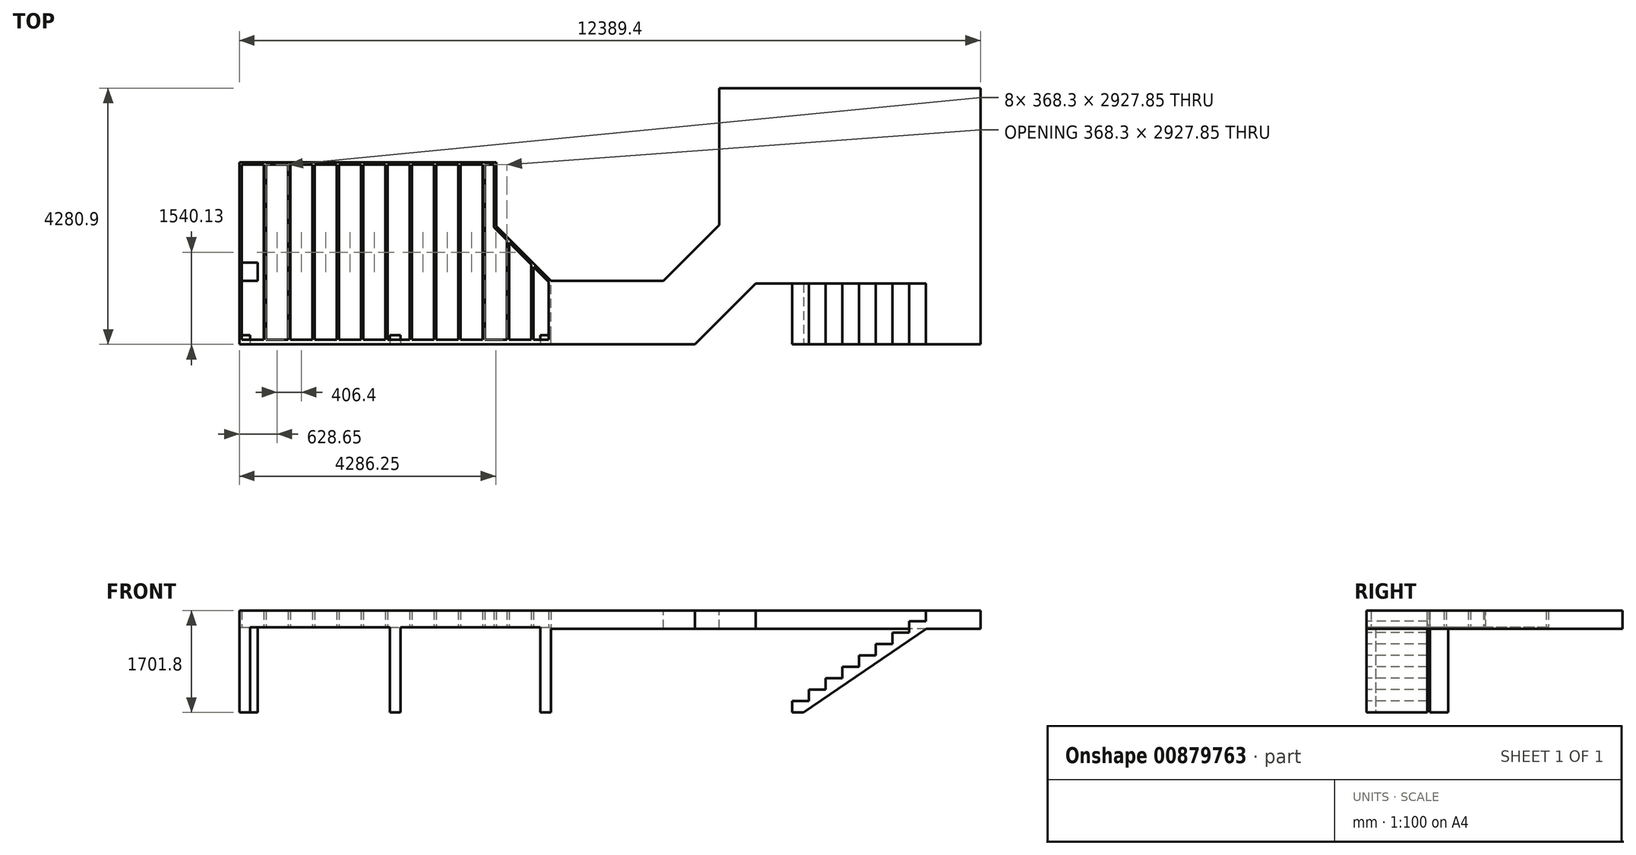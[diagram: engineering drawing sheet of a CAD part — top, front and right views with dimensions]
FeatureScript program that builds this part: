
annotation { "Feature Type Name" : "Feature", "Feature Type Description" : "" }
export const myFeature = defineFeature(function(context is Context, id is Id, definition is map)
    precondition{}
    {
        {
            var Q0;
            Q0=qCreatedBy(makeId("Top.planeOp"),FACE);
            var sketch = newSketch(context, id + "F0", { "sketchPlane" : qUnion([Q0])});
            skLineSegment(sketch, "E0.bottom", {"start": v(0, -1676.4) * mm, "end": v(304.8, -1676.4) * mm});
            skLineSegment(sketch, "E0.top", {"start": v(0, -1981.2) * mm, "end": v(304.8, -1981.2) * mm});
            skLineSegment(sketch, "E0.left", {"start": v(0, -1676.4) * mm, "end": v(0, -1981.2) * mm});
            skLineSegment(sketch, "E0.right", {"start": v(304.8, -1676.4) * mm, "end": v(304.8, -1981.2) * mm});
            skLineSegment(sketch, "E1.bottom", {"start": v(0, -2889.75) * mm, "end": v(177.8, -2889.75) * mm});
            skLineSegment(sketch, "E1.top", {"start": v(0, -3042.15) * mm, "end": v(177.8, -3042.15) * mm});
            skLineSegment(sketch, "E1.left", {"start": v(0, -2889.75) * mm, "end": v(0, -3042.15) * mm});
            skLineSegment(sketch, "E1.right", {"start": v(177.8, -2889.75) * mm, "end": v(177.8, -3042.15) * mm});
            skLineSegment(sketch, "E2.bottom", {"start": v(2514.6, -2889.75) * mm, "end": v(2692.4, -2889.75) * mm});
            skLineSegment(sketch, "E2.top", {"start": v(2514.6, -3042.15) * mm, "end": v(2692.4, -3042.15) * mm});
            skLineSegment(sketch, "E2.left", {"start": v(2514.6, -2889.75) * mm, "end": v(2514.6, -3042.15) * mm});
            skLineSegment(sketch, "E2.right", {"start": v(2692.4, -2889.75) * mm, "end": v(2692.4, -3042.15) * mm});
            skLineSegment(sketch, "E3.bottom", {"start": v(5029.2, -2889.75) * mm, "end": v(5207, -2889.75) * mm});
            skLineSegment(sketch, "E3.top", {"start": v(5029.2, -3042.15) * mm, "end": v(5207, -3042.15) * mm});
            skLineSegment(sketch, "E3.left", {"start": v(5029.2, -2889.75) * mm, "end": v(5029.2, -3042.15) * mm});
            skLineSegment(sketch, "E3.right", {"start": v(5207, -2889.75) * mm, "end": v(5207, -3042.15) * mm});
            skLineSegment(sketch, "E4", {"start": v(0, 0) * mm, "end": v(4292.6, 0) * mm, "construction": true});
            skLineSegment(sketch, "E5", {"start": v(4292.6, 0) * mm, "end": v(4292.6, -1066.8) * mm, "construction": true});
            skLineSegment(sketch, "E6", {"start": v(4292.6, -1066.8) * mm, "end": v(5226.55, -2000.75) * mm, "construction": true});
            skLineSegment(sketch, "E7", {"start": v(5226.55, -2000.75) * mm, "end": v(7106.15, -2000.75) * mm, "construction": true});
            skSolve(sketch);
        }
        {
            var Q0;
            Q0=qSketchRegion(id+"F0",true);
            extrude(context, id + "F1", {"entities" : qUnion([Q0]), "depth" : 1422.4 * mm, "offsetDistance" : 25.4 * mm});
        }
        {
            var Q0;
            Q0=makeQuery(id+"F1.opExtrude","CAP_FACE",FACE,{"disambiguationData":[OSD([sQuery(id+"F0.wireOp",EDGE,"E0.bottom"),sQuery(id+"F0.wireOp",EDGE,"E0.top"),sQuery(id+"F0.wireOp",EDGE,"E0.left"),sQuery(id+"F0.wireOp",EDGE,"E0.right")])],"isStart":false});
            var sketch = newSketch(context, id + "F2", { "sketchPlane" : qUnion([Q0])});
            skLineSegment(sketch, "E8.0", {"start": v(0, 0) * mm, "end": v(4292.6, 0) * mm});
            skLineSegment(sketch, "E9.0", {"start": v(4292.6, 0) * mm, "end": v(4292.6, -1066.8) * mm});
            skLineSegment(sketch, "E9.1", {"start": v(4292.6, -1066.8) * mm, "end": v(5207, -1981.2) * mm});
            skLineSegment(sketch, "E10", {"start": v(0, 0) * mm, "end": v(0, -3042.15) * mm});
            skLineSegment(sketch, "E11", {"start": v(0, -3042.15) * mm, "end": v(5207, -3042.15) * mm});
            skLineSegment(sketch, "E12", {"start": v(5207, -3042.15) * mm, "end": v(5207, -1981.2) * mm});
            skPoint(sketch, "E13.orphan", {"position": v(5226.55, -2000.75) * mm});
            skLineSegment(sketch, "E14.0", {"start": v(4254.5, -38.1) * mm, "end": v(4254.5, -1082.58) * mm});
            skLineSegment(sketch, "E14.1", {"start": v(5168.9, -3004.05) * mm, "end": v(5168.9, -1996.98) * mm});
            skLineSegment(sketch, "E14.2", {"start": v(38.1, -3004.05) * mm, "end": v(5168.9, -3004.05) * mm});
            skLineSegment(sketch, "E14.3", {"start": v(4254.5, -1082.58) * mm, "end": v(5168.9, -1996.98) * mm});
            skLineSegment(sketch, "E14.4", {"start": v(38.1, -38.1) * mm, "end": v(38.1, -3004.05) * mm});
            skLineSegment(sketch, "E14.5", {"start": v(38.1, -38.1) * mm, "end": v(4254.5, -38.1) * mm});
            skSolve(sketch);
        }
        {
            var Q0;
            Q0=qSketchRegion(id+"F2",true);
            extrude(context, id + "F3", {"entities" : qUnion([Q0]), "operationType" : NewBodyOperationType.ADD, "depth" : 279.4 * mm, "offsetDistance" : 25.4 * mm});
        }
        {
            var Q0;
            Q0=makeQuery(id+"F1.opExtrude","CAP_FACE",FACE,{"disambiguationData":[OSD([sQuery(id+"F0.wireOp",EDGE,"E1.bottom"),sQuery(id+"F0.wireOp",EDGE,"E1.top"),sQuery(id+"F0.wireOp",EDGE,"E1.left"),sQuery(id+"F0.wireOp",EDGE,"E1.right")])],"isStart":false});
            var sketch = newSketch(context, id + "F4", { "sketchPlane" : qUnion([Q0])});
            skPoint(sketch, "E15.oppositeSnap0", {"position": v(38.1, -2965.95) * mm});
            skLineSegment(sketch, "E15.bottom", {"start": v(38.1, -3004.05) * mm, "end": v(5168.9, -3004.05) * mm});
            skLineSegment(sketch, "E15.top", {"start": v(38.1, -2965.95) * mm, "end": v(5168.9, -2965.95) * mm});
            skLineSegment(sketch, "E15.left", {"start": v(38.1, -3004.05) * mm, "end": v(38.1, -2965.95) * mm});
            skLineSegment(sketch, "E15.right", {"start": v(5168.9, -3004.05) * mm, "end": v(5168.9, -2965.95) * mm});
            skSolve(sketch);
        }
        {
            var Q0;
            Q0=qSketchRegion(id+"F4",true);
            var Q1;
            Q1=makeQuery(id+"F3.opExtrude","CAP_FACE",FACE,{"disambiguationData":[OSD([sQuery(id+"F2.wireOp",EDGE,"E8.0"),sQuery(id+"F2.wireOp",EDGE,"E9.0"),sQuery(id+"F2.wireOp",EDGE,"E9.1"),sQuery(id+"F2.wireOp",EDGE,"E10"),sQuery(id+"F2.wireOp",EDGE,"E11"),sQuery(id+"F2.wireOp",EDGE,"E12"),sQuery(id+"F2.wireOp",EDGE,"E14.0"),sQuery(id+"F2.wireOp",EDGE,"E14.1"),sQuery(id+"F2.wireOp",EDGE,"E14.2"),sQuery(id+"F2.wireOp",EDGE,"E14.3"),sQuery(id+"F2.wireOp",EDGE,"E14.4"),sQuery(id+"F2.wireOp",EDGE,"E14.5")])],"isStart":false});
            extrude(context, id + "F5", {"entities" : qUnion([Q0]), "operationType" : NewBodyOperationType.ADD, "endBound" : BoundingType.UP_TO_SURFACE, "depth" : 25.4 * mm, "endBoundEntityFace" : qUnion([Q1]), "offsetDistance" : 25.4 * mm});
        }
        {
            var Q0;
            Q0=makeQuery(id+"F1.opExtrude","CAP_FACE",FACE,{"disambiguationData":[OSD([sQuery(id+"F0.wireOp",EDGE,"E0.bottom"),sQuery(id+"F0.wireOp",EDGE,"E0.top"),sQuery(id+"F0.wireOp",EDGE,"E0.left"),sQuery(id+"F0.wireOp",EDGE,"E0.right")])],"isStart":false});
            var sketch = newSketch(context, id + "F6", { "sketchPlane" : qUnion([Q0])});
            skLineSegment(sketch, "E16.bottom", {"start": v(406.4, -38.1) * mm, "end": v(444.5, -38.1) * mm});
            skLineSegment(sketch, "E16.top", {"start": v(406.4, -2965.95) * mm, "end": v(444.5, -2965.95) * mm});
            skLineSegment(sketch, "E16.left", {"start": v(406.4, -38.1) * mm, "end": v(406.4, -2965.95) * mm});
            skLineSegment(sketch, "E16.right", {"start": v(444.5, -38.1) * mm, "end": v(444.5, -2965.95) * mm});
            skLineSegment(sketch, "E17.1.0.0", {"start": v(850.9, -38.1) * mm, "end": v(850.9, -2965.95) * mm});
            skLineSegment(sketch, "E17.1.0.1", {"start": v(812.8, -38.1) * mm, "end": v(812.8, -2965.95) * mm});
            skLineSegment(sketch, "E17.1.0.2", {"start": v(812.8, -38.1) * mm, "end": v(850.9, -38.1) * mm});
            skLineSegment(sketch, "E17.1.0.3", {"start": v(812.8, -2965.95) * mm, "end": v(850.9, -2965.95) * mm});
            skLineSegment(sketch, "E17.2.0.0", {"start": v(1257.3, -38.1) * mm, "end": v(1257.3, -2965.95) * mm});
            skLineSegment(sketch, "E17.2.0.1", {"start": v(1219.2, -38.1) * mm, "end": v(1219.2, -2965.95) * mm});
            skLineSegment(sketch, "E17.2.0.2", {"start": v(1219.2, -38.1) * mm, "end": v(1257.3, -38.1) * mm});
            skLineSegment(sketch, "E17.2.0.3", {"start": v(1219.2, -2965.95) * mm, "end": v(1257.3, -2965.95) * mm});
            skLineSegment(sketch, "E17.3.0.0", {"start": v(1663.7, -38.1) * mm, "end": v(1663.7, -2965.95) * mm});
            skLineSegment(sketch, "E17.3.0.1", {"start": v(1625.6, -38.1) * mm, "end": v(1625.6, -2965.95) * mm});
            skLineSegment(sketch, "E17.3.0.2", {"start": v(1625.6, -38.1) * mm, "end": v(1663.7, -38.1) * mm});
            skLineSegment(sketch, "E17.3.0.3", {"start": v(1625.6, -2965.95) * mm, "end": v(1663.7, -2965.95) * mm});
            skLineSegment(sketch, "E17.4.0.0", {"start": v(2070.1, -38.1) * mm, "end": v(2070.1, -2965.95) * mm});
            skLineSegment(sketch, "E17.4.0.1", {"start": v(2032, -38.1) * mm, "end": v(2032, -2965.95) * mm});
            skLineSegment(sketch, "E17.4.0.2", {"start": v(2032, -38.1) * mm, "end": v(2070.1, -38.1) * mm});
            skLineSegment(sketch, "E17.4.0.3", {"start": v(2032, -2965.95) * mm, "end": v(2070.1, -2965.95) * mm});
            skLineSegment(sketch, "E17.5.0.0", {"start": v(2476.5, -38.1) * mm, "end": v(2476.5, -2965.95) * mm});
            skLineSegment(sketch, "E17.5.0.1", {"start": v(2438.4, -38.1) * mm, "end": v(2438.4, -2965.95) * mm});
            skLineSegment(sketch, "E17.5.0.2", {"start": v(2438.4, -38.1) * mm, "end": v(2476.5, -38.1) * mm});
            skLineSegment(sketch, "E17.5.0.3", {"start": v(2438.4, -2965.95) * mm, "end": v(2476.5, -2965.95) * mm});
            skLineSegment(sketch, "E17.6.0.0", {"start": v(2882.9, -38.1) * mm, "end": v(2882.9, -2965.95) * mm});
            skLineSegment(sketch, "E17.6.0.1", {"start": v(2844.8, -38.1) * mm, "end": v(2844.8, -2965.95) * mm});
            skLineSegment(sketch, "E17.6.0.2", {"start": v(2844.8, -38.1) * mm, "end": v(2882.9, -38.1) * mm});
            skLineSegment(sketch, "E17.6.0.3", {"start": v(2844.8, -2965.95) * mm, "end": v(2882.9, -2965.95) * mm});
            skLineSegment(sketch, "E17.7.0.0", {"start": v(3289.3, -38.1) * mm, "end": v(3289.3, -2965.95) * mm});
            skLineSegment(sketch, "E17.7.0.1", {"start": v(3251.2, -38.1) * mm, "end": v(3251.2, -2965.95) * mm});
            skLineSegment(sketch, "E17.7.0.2", {"start": v(3251.2, -38.1) * mm, "end": v(3289.3, -38.1) * mm});
            skLineSegment(sketch, "E17.7.0.3", {"start": v(3251.2, -2965.95) * mm, "end": v(3289.3, -2965.95) * mm});
            skLineSegment(sketch, "E17.8.0.0", {"start": v(3695.7, -38.1) * mm, "end": v(3695.7, -2965.95) * mm});
            skLineSegment(sketch, "E17.8.0.1", {"start": v(3657.6, -38.1) * mm, "end": v(3657.6, -2965.95) * mm});
            skLineSegment(sketch, "E17.8.0.2", {"start": v(3657.6, -38.1) * mm, "end": v(3695.7, -38.1) * mm});
            skLineSegment(sketch, "E17.8.0.3", {"start": v(3657.6, -2965.95) * mm, "end": v(3695.7, -2965.95) * mm});
            skLineSegment(sketch, "E17.9.0.0", {"start": v(4102.1, -38.1) * mm, "end": v(4102.1, -2965.95) * mm});
            skLineSegment(sketch, "E17.9.0.1", {"start": v(4064, -38.1) * mm, "end": v(4064, -2965.95) * mm});
            skLineSegment(sketch, "E17.9.0.2", {"start": v(4064, -38.1) * mm, "end": v(4102.1, -38.1) * mm});
            skLineSegment(sketch, "E17.9.0.3", {"start": v(4064, -2965.95) * mm, "end": v(4102.1, -2965.95) * mm});
            skLineSegment(sketch, "E17.direction1", {"start": v(406.4, -2965.95) * mm, "end": v(812.8, -2965.95) * mm, "construction": true});
            skLineSegment(sketch, "E18.top", {"start": v(4470.4, -2965.95) * mm, "end": v(4508.5, -2965.95) * mm});
            skLineSegment(sketch, "E18.left", {"start": v(4470.4, -1298.48) * mm, "end": v(4470.4, -2965.95) * mm});
            skLineSegment(sketch, "E18.right", {"start": v(4508.5, -1336.58) * mm, "end": v(4508.5, -2965.95) * mm});
            skLineSegment(sketch, "E19.top", {"start": v(4876.8, -2965.95) * mm, "end": v(4914.9, -2965.95) * mm});
            skLineSegment(sketch, "E19.left", {"start": v(4876.8, -1704.88) * mm, "end": v(4876.8, -2965.95) * mm});
            skLineSegment(sketch, "E19.right", {"start": v(4914.9, -1742.98) * mm, "end": v(4914.9, -2965.95) * mm});
            skLineSegment(sketch, "E20", {"start": v(4470.4, -1298.48) * mm, "end": v(4508.5, -1336.58) * mm});
            skLineSegment(sketch, "E21.trimOffspring", {"start": v(4876.8, -1704.88) * mm, "end": v(4914.9, -1742.98) * mm});
            skSolve(sketch);
        }
        {
            var Q0;
            Q0=qSketchRegion(id+"F6",true);
            var Q1;
            {var subQ0=sQuery(id+"F2.wireOp",EDGE,"E14.5");var subQ1=sQuery(id+"F2.wireOp",EDGE,"E14.4");var subQ2=sQuery(id+"F2.wireOp",EDGE,"E14.3");var subQ3=sQuery(id+"F2.wireOp",EDGE,"E14.2");var subQ4=sQuery(id+"F2.wireOp",EDGE,"E14.1");var subQ5=sQuery(id+"F2.wireOp",EDGE,"E14.0");var subQ6=sQuery(id+"F2.wireOp",EDGE,"E12");var subQ7=sQuery(id+"F2.wireOp",EDGE,"E11");var subQ8=sQuery(id+"F2.wireOp",EDGE,"E10");var subQ9=sQuery(id+"F2.wireOp",EDGE,"E9.1");var subQ10=sQuery(id+"F2.wireOp",EDGE,"E9.0");var subQ11=sQuery(id+"F2.wireOp",EDGE,"E8.0");Q1=makeQuery(id+"F5.boolean.opBoolean","MERGE",FACE,{"derivedFrom":[makeQuery(id+"F3.opExtrude","CAP_FACE",FACE,{"disambiguationData":[OSD([subQ11,subQ10,subQ9,subQ8,subQ7,subQ6,subQ5,subQ4,subQ3,subQ2,subQ1,subQ0])],"isStart":false}),makeQuery(id+"F5.opExtrude","CAP_FACE",FACE,{"disambiguationData":[OSD([subQ11,subQ10,subQ9,subQ8,subQ7,subQ6,subQ5,subQ4,subQ3,subQ2,subQ1,subQ0])],"isStart":false})]});}
            extrude(context, id + "F7", {"entities" : qUnion([Q0]), "operationType" : NewBodyOperationType.ADD, "endBound" : BoundingType.UP_TO_SURFACE, "depth" : 25.4 * mm, "endBoundEntityFace" : qUnion([Q1]), "offsetDistance" : 25.4 * mm});
        }
        {
            var Q0;
            Q0=makeQuery(id+"F7.boolean.opBoolean","MERGE",FACE,{"derivedFrom":[makeQuery(id+"F5.boolean.opBoolean","MERGE",FACE,{"derivedFrom":[makeQuery(id+"F3.opExtrude","CAP_FACE",FACE,{"disambiguationData":[OSD([sQuery(id+"F2.wireOp",EDGE,"E8.0"),sQuery(id+"F2.wireOp",EDGE,"E9.0"),sQuery(id+"F2.wireOp",EDGE,"E9.1"),sQuery(id+"F2.wireOp",EDGE,"E10"),sQuery(id+"F2.wireOp",EDGE,"E11"),sQuery(id+"F2.wireOp",EDGE,"E12"),sQuery(id+"F2.wireOp",EDGE,"E14.0"),sQuery(id+"F2.wireOp",EDGE,"E14.1"),sQuery(id+"F2.wireOp",EDGE,"E14.2"),sQuery(id+"F2.wireOp",EDGE,"E14.3"),sQuery(id+"F2.wireOp",EDGE,"E14.4"),sQuery(id+"F2.wireOp",EDGE,"E14.5")])],"isStart":false}),makeQuery(id+"F5.opExtrude","CAP_FACE",FACE,{"disambiguationData":[OSD([sQuery(id+"F4.wireOp",EDGE,"E15.bottom"),sQuery(id+"F4.wireOp",EDGE,"E15.top"),sQuery(id+"F4.wireOp",EDGE,"E15.left"),sQuery(id+"F4.wireOp",EDGE,"E15.right")])],"isStart":false})]}),makeQuery(id+"F7.opExtrude","CAP_FACE",FACE,{"disambiguationData":[OSD([sQuery(id+"F6.wireOp",EDGE,"E16.bottom"),sQuery(id+"F6.wireOp",EDGE,"E16.top"),sQuery(id+"F6.wireOp",EDGE,"E16.left"),sQuery(id+"F6.wireOp",EDGE,"E16.right")])],"isStart":false}),makeQuery(id+"F7.opExtrude","CAP_FACE",FACE,{"disambiguationData":[OSD([sQuery(id+"F6.wireOp",EDGE,"E17.1.0.0"),sQuery(id+"F6.wireOp",EDGE,"E17.1.0.1"),sQuery(id+"F6.wireOp",EDGE,"E17.1.0.2"),sQuery(id+"F6.wireOp",EDGE,"E17.1.0.3")])],"isStart":false}),makeQuery(id+"F7.opExtrude","CAP_FACE",FACE,{"disambiguationData":[OSD([sQuery(id+"F6.wireOp",EDGE,"E17.2.0.0"),sQuery(id+"F6.wireOp",EDGE,"E17.2.0.1"),sQuery(id+"F6.wireOp",EDGE,"E17.2.0.2"),sQuery(id+"F6.wireOp",EDGE,"E17.2.0.3")])],"isStart":false}),makeQuery(id+"F7.opExtrude","CAP_FACE",FACE,{"disambiguationData":[OSD([sQuery(id+"F6.wireOp",EDGE,"E17.3.0.0"),sQuery(id+"F6.wireOp",EDGE,"E17.3.0.1"),sQuery(id+"F6.wireOp",EDGE,"E17.3.0.2"),sQuery(id+"F6.wireOp",EDGE,"E17.3.0.3")])],"isStart":false}),makeQuery(id+"F7.opExtrude","CAP_FACE",FACE,{"disambiguationData":[OSD([sQuery(id+"F6.wireOp",EDGE,"E17.4.0.0"),sQuery(id+"F6.wireOp",EDGE,"E17.4.0.1"),sQuery(id+"F6.wireOp",EDGE,"E17.4.0.2"),sQuery(id+"F6.wireOp",EDGE,"E17.4.0.3")])],"isStart":false}),makeQuery(id+"F7.opExtrude","CAP_FACE",FACE,{"disambiguationData":[OSD([sQuery(id+"F6.wireOp",EDGE,"E17.5.0.0"),sQuery(id+"F6.wireOp",EDGE,"E17.5.0.1"),sQuery(id+"F6.wireOp",EDGE,"E17.5.0.2"),sQuery(id+"F6.wireOp",EDGE,"E17.5.0.3")])],"isStart":false}),makeQuery(id+"F7.opExtrude","CAP_FACE",FACE,{"disambiguationData":[OSD([sQuery(id+"F6.wireOp",EDGE,"E17.6.0.0"),sQuery(id+"F6.wireOp",EDGE,"E17.6.0.1"),sQuery(id+"F6.wireOp",EDGE,"E17.6.0.2"),sQuery(id+"F6.wireOp",EDGE,"E17.6.0.3")])],"isStart":false}),makeQuery(id+"F7.opExtrude","CAP_FACE",FACE,{"disambiguationData":[OSD([sQuery(id+"F6.wireOp",EDGE,"E17.7.0.0"),sQuery(id+"F6.wireOp",EDGE,"E17.7.0.1"),sQuery(id+"F6.wireOp",EDGE,"E17.7.0.2"),sQuery(id+"F6.wireOp",EDGE,"E17.7.0.3")])],"isStart":false}),makeQuery(id+"F7.opExtrude","CAP_FACE",FACE,{"disambiguationData":[OSD([sQuery(id+"F6.wireOp",EDGE,"E17.8.0.0"),sQuery(id+"F6.wireOp",EDGE,"E17.8.0.1"),sQuery(id+"F6.wireOp",EDGE,"E17.8.0.2"),sQuery(id+"F6.wireOp",EDGE,"E17.8.0.3")])],"isStart":false}),makeQuery(id+"F7.opExtrude","CAP_FACE",FACE,{"disambiguationData":[OSD([sQuery(id+"F6.wireOp",EDGE,"E17.9.0.0"),sQuery(id+"F6.wireOp",EDGE,"E17.9.0.1"),sQuery(id+"F6.wireOp",EDGE,"E17.9.0.2"),sQuery(id+"F6.wireOp",EDGE,"E17.9.0.3")])],"isStart":false}),makeQuery(id+"F7.opExtrude","CAP_FACE",FACE,{"disambiguationData":[OSD([sQuery(id+"F6.wireOp",EDGE,"E18.top"),sQuery(id+"F6.wireOp",EDGE,"E18.left"),sQuery(id+"F6.wireOp",EDGE,"E18.right"),sQuery(id+"F6.wireOp",EDGE,"E20")])],"isStart":false}),makeQuery(id+"F7.opExtrude","CAP_FACE",FACE,{"disambiguationData":[OSD([sQuery(id+"F6.wireOp",EDGE,"E19.top"),sQuery(id+"F6.wireOp",EDGE,"E19.left"),sQuery(id+"F6.wireOp",EDGE,"E19.right"),sQuery(id+"F6.wireOp",EDGE,"E21.trimOffspring")])],"isStart":false})]});
            var sketch = newSketch(context, id + "F8", { "sketchPlane" : qUnion([Q0])});
            skLineSegment(sketch, "E22", {"start": v(5207, -1981.2) * mm, "end": v(5207, -3042.15) * mm});
            skLineSegment(sketch, "E23", {"start": v(5207, -1981.2) * mm, "end": v(7086.6, -1981.2) * mm});
            skLineSegment(sketch, "E24", {"start": v(7086.6, -1981.2) * mm, "end": v(8020.55, -1047.25) * mm});
            skLineSegment(sketch, "E25", {"start": v(8020.55, -1047.25) * mm, "end": v(8020.55, 1238.75) * mm});
            skLineSegment(sketch, "E26", {"start": v(8020.55, 1238.75) * mm, "end": v(12389.35, 1238.75) * mm});
            skLineSegment(sketch, "E27", {"start": v(12389.35, 1238.75) * mm, "end": v(12389.35, -3042.15) * mm});
            skLineSegment(sketch, "E28", {"start": v(5207, -3042.15) * mm, "end": v(12389.35, -3042.15) * mm});
            skSolve(sketch);
        }
        {
            var Q0;
            Q0=qSketchRegion(id+"F8",true);
            extrude(context, id + "F9", {"entities" : qUnion([Q0]), "operationType" : NewBodyOperationType.ADD, "oppositeDirection" : true, "depth" : 304.8 * mm, "offsetDistance" : 25.4 * mm});
        }
        {
            var Q0;
            Q0=makeQuery(id+"F9.boolean.opBoolean","MERGE",FACE,{"derivedFrom":[makeQuery(id+"F7.boolean.opBoolean","MERGE",FACE,{"derivedFrom":[makeQuery(id+"F5.boolean.opBoolean","MERGE",FACE,{"derivedFrom":[makeQuery(id+"F3.opExtrude","CAP_FACE",FACE,{"disambiguationData":[OSD([sQuery(id+"F2.wireOp",EDGE,"E8.0"),sQuery(id+"F2.wireOp",EDGE,"E9.0"),sQuery(id+"F2.wireOp",EDGE,"E9.1"),sQuery(id+"F2.wireOp",EDGE,"E10"),sQuery(id+"F2.wireOp",EDGE,"E11"),sQuery(id+"F2.wireOp",EDGE,"E12"),sQuery(id+"F2.wireOp",EDGE,"E14.0"),sQuery(id+"F2.wireOp",EDGE,"E14.1"),sQuery(id+"F2.wireOp",EDGE,"E14.2"),sQuery(id+"F2.wireOp",EDGE,"E14.3"),sQuery(id+"F2.wireOp",EDGE,"E14.4"),sQuery(id+"F2.wireOp",EDGE,"E14.5")])],"isStart":false}),makeQuery(id+"F5.opExtrude","CAP_FACE",FACE,{"disambiguationData":[OSD([sQuery(id+"F4.wireOp",EDGE,"E15.bottom"),sQuery(id+"F4.wireOp",EDGE,"E15.top"),sQuery(id+"F4.wireOp",EDGE,"E15.left"),sQuery(id+"F4.wireOp",EDGE,"E15.right")])],"isStart":false})]}),makeQuery(id+"F7.opExtrude","CAP_FACE",FACE,{"disambiguationData":[OSD([sQuery(id+"F6.wireOp",EDGE,"E16.bottom"),sQuery(id+"F6.wireOp",EDGE,"E16.top"),sQuery(id+"F6.wireOp",EDGE,"E16.left"),sQuery(id+"F6.wireOp",EDGE,"E16.right")])],"isStart":false}),makeQuery(id+"F7.opExtrude","CAP_FACE",FACE,{"disambiguationData":[OSD([sQuery(id+"F6.wireOp",EDGE,"E17.1.0.0"),sQuery(id+"F6.wireOp",EDGE,"E17.1.0.1"),sQuery(id+"F6.wireOp",EDGE,"E17.1.0.2"),sQuery(id+"F6.wireOp",EDGE,"E17.1.0.3")])],"isStart":false}),makeQuery(id+"F7.opExtrude","CAP_FACE",FACE,{"disambiguationData":[OSD([sQuery(id+"F6.wireOp",EDGE,"E17.2.0.0"),sQuery(id+"F6.wireOp",EDGE,"E17.2.0.1"),sQuery(id+"F6.wireOp",EDGE,"E17.2.0.2"),sQuery(id+"F6.wireOp",EDGE,"E17.2.0.3")])],"isStart":false}),makeQuery(id+"F7.opExtrude","CAP_FACE",FACE,{"disambiguationData":[OSD([sQuery(id+"F6.wireOp",EDGE,"E17.3.0.0"),sQuery(id+"F6.wireOp",EDGE,"E17.3.0.1"),sQuery(id+"F6.wireOp",EDGE,"E17.3.0.2"),sQuery(id+"F6.wireOp",EDGE,"E17.3.0.3")])],"isStart":false}),makeQuery(id+"F7.opExtrude","CAP_FACE",FACE,{"disambiguationData":[OSD([sQuery(id+"F6.wireOp",EDGE,"E17.4.0.0"),sQuery(id+"F6.wireOp",EDGE,"E17.4.0.1"),sQuery(id+"F6.wireOp",EDGE,"E17.4.0.2"),sQuery(id+"F6.wireOp",EDGE,"E17.4.0.3")])],"isStart":false}),makeQuery(id+"F7.opExtrude","CAP_FACE",FACE,{"disambiguationData":[OSD([sQuery(id+"F6.wireOp",EDGE,"E17.5.0.0"),sQuery(id+"F6.wireOp",EDGE,"E17.5.0.1"),sQuery(id+"F6.wireOp",EDGE,"E17.5.0.2"),sQuery(id+"F6.wireOp",EDGE,"E17.5.0.3")])],"isStart":false}),makeQuery(id+"F7.opExtrude","CAP_FACE",FACE,{"disambiguationData":[OSD([sQuery(id+"F6.wireOp",EDGE,"E17.6.0.0"),sQuery(id+"F6.wireOp",EDGE,"E17.6.0.1"),sQuery(id+"F6.wireOp",EDGE,"E17.6.0.2"),sQuery(id+"F6.wireOp",EDGE,"E17.6.0.3")])],"isStart":false}),makeQuery(id+"F7.opExtrude","CAP_FACE",FACE,{"disambiguationData":[OSD([sQuery(id+"F6.wireOp",EDGE,"E17.7.0.0"),sQuery(id+"F6.wireOp",EDGE,"E17.7.0.1"),sQuery(id+"F6.wireOp",EDGE,"E17.7.0.2"),sQuery(id+"F6.wireOp",EDGE,"E17.7.0.3")])],"isStart":false}),makeQuery(id+"F7.opExtrude","CAP_FACE",FACE,{"disambiguationData":[OSD([sQuery(id+"F6.wireOp",EDGE,"E17.8.0.0"),sQuery(id+"F6.wireOp",EDGE,"E17.8.0.1"),sQuery(id+"F6.wireOp",EDGE,"E17.8.0.2"),sQuery(id+"F6.wireOp",EDGE,"E17.8.0.3")])],"isStart":false}),makeQuery(id+"F7.opExtrude","CAP_FACE",FACE,{"disambiguationData":[OSD([sQuery(id+"F6.wireOp",EDGE,"E17.9.0.0"),sQuery(id+"F6.wireOp",EDGE,"E17.9.0.1"),sQuery(id+"F6.wireOp",EDGE,"E17.9.0.2"),sQuery(id+"F6.wireOp",EDGE,"E17.9.0.3")])],"isStart":false}),makeQuery(id+"F7.opExtrude","CAP_FACE",FACE,{"disambiguationData":[OSD([sQuery(id+"F6.wireOp",EDGE,"E18.top"),sQuery(id+"F6.wireOp",EDGE,"E18.left"),sQuery(id+"F6.wireOp",EDGE,"E18.right"),sQuery(id+"F6.wireOp",EDGE,"E20")])],"isStart":false}),makeQuery(id+"F7.opExtrude","CAP_FACE",FACE,{"disambiguationData":[OSD([sQuery(id+"F6.wireOp",EDGE,"E19.top"),sQuery(id+"F6.wireOp",EDGE,"E19.left"),sQuery(id+"F6.wireOp",EDGE,"E19.right"),sQuery(id+"F6.wireOp",EDGE,"E21.trimOffspring")])],"isStart":false})]}),makeQuery(id+"F9.opExtrude","CAP_FACE",FACE,{"disambiguationData":[OSD([sQuery(id+"F8.wireOp",EDGE,"E22"),sQuery(id+"F8.wireOp",EDGE,"E23"),sQuery(id+"F8.wireOp",EDGE,"E24"),sQuery(id+"F8.wireOp",EDGE,"E25"),sQuery(id+"F8.wireOp",EDGE,"E26"),sQuery(id+"F8.wireOp",EDGE,"E27"),sQuery(id+"F8.wireOp",EDGE,"E28")])],"isStart":true})]});
            var sketch = newSketch(context, id + "F10", { "sketchPlane" : qUnion([Q0])});
            skLineSegment(sketch, "E29.bottom", {"start": v(11474.95, -3042.15) * mm, "end": v(9239.75, -3042.15) * mm});
            skLineSegment(sketch, "E29.top", {"start": v(11474.95, -2026.15) * mm, "end": v(9239.75, -2026.15) * mm});
            skLineSegment(sketch, "E29.left", {"start": v(11474.95, -3042.15) * mm, "end": v(11474.95, -2026.15) * mm});
            skLineSegment(sketch, "E29.right", {"start": v(9239.75, -3042.15) * mm, "end": v(9239.75, -2026.15) * mm});
            skSolve(sketch);
        }
        {
            var Q0;
            Q0=qSketchRegion(id+"F10",true);
            extrude(context, id + "F11", {"entities" : qUnion([Q0]), "operationType" : NewBodyOperationType.REMOVE, "endBound" : BoundingType.THROUGH_ALL, "oppositeDirection" : true, "depth" : 25.4 * mm, "offsetDistance" : 25.4 * mm});
        }
        {
            var Q0;
            Q0=makeQuery(id+"F9.boolean.opBoolean","MERGE",FACE,{"derivedFrom":[makeQuery(id+"F3.boolean.opBoolean","MERGE",FACE,{"derivedFrom":[makeQuery(id+"F1.opExtrude","SWEPT_FACE",FACE,{"disambiguationData":[OSD([sQuery(id+"F0.wireOp",EDGE,"E1.top")])]}),makeQuery(id+"F1.opExtrude","SWEPT_FACE",FACE,{"disambiguationData":[OSD([sQuery(id+"F0.wireOp",EDGE,"E2.top")])]}),makeQuery(id+"F1.opExtrude","SWEPT_FACE",FACE,{"disambiguationData":[OSD([sQuery(id+"F0.wireOp",EDGE,"E3.top")])]}),makeQuery(id+"F3.opExtrude","SWEPT_FACE",FACE,{"disambiguationData":[OSD([sQuery(id+"F2.wireOp",EDGE,"E11")])]})]}),makeQuery(id+"F9.opExtrude","SWEPT_FACE",FACE,{"disambiguationData":[OSD([sQuery(id+"F8.wireOp",EDGE,"E28")])]})]});
            var sketch = newSketch(context, id + "F12", { "sketchPlane" : qUnion([Q0])});
            skLineSegment(sketch, "E30", {"start": v(11195.55, 1524) * mm, "end": v(11474.95, 1524) * mm});
            skLineSegment(sketch, "E31", {"start": v(11195.55, 1524) * mm, "end": v(11195.55, 1333.5) * mm});
            skLineSegment(sketch, "E32", {"start": v(10916.15, 1333.5) * mm, "end": v(11195.55, 1333.5) * mm});
            skLineSegment(sketch, "E33", {"start": v(10916.15, 1333.5) * mm, "end": v(10916.15, 1143) * mm});
            skLineSegment(sketch, "E34", {"start": v(10636.75, 1143) * mm, "end": v(10916.15, 1143) * mm});
            skLineSegment(sketch, "E35", {"start": v(10636.75, 1143) * mm, "end": v(10636.75, 952.5) * mm});
            skLineSegment(sketch, "E36", {"start": v(10357.35, 952.5) * mm, "end": v(10636.75, 952.5) * mm});
            skLineSegment(sketch, "E37", {"start": v(10357.35, 952.5) * mm, "end": v(10357.35, 762) * mm});
            skLineSegment(sketch, "E38", {"start": v(10077.95, 762) * mm, "end": v(10357.35, 762) * mm});
            skLineSegment(sketch, "E39", {"start": v(10077.95, 762) * mm, "end": v(10077.95, 571.5) * mm});
            skLineSegment(sketch, "E40", {"start": v(9798.55, 571.5) * mm, "end": v(10077.95, 571.5) * mm});
            skLineSegment(sketch, "E41", {"start": v(9798.55, 571.5) * mm, "end": v(9798.55, 381) * mm});
            skLineSegment(sketch, "E42", {"start": v(9519.15, 381) * mm, "end": v(9798.55, 381) * mm});
            skLineSegment(sketch, "E43", {"start": v(9519.15, 381) * mm, "end": v(9519.15, 190.5) * mm});
            skLineSegment(sketch, "E44", {"start": v(9239.75, 190.5) * mm, "end": v(9519.15, 190.5) * mm});
            skLineSegment(sketch, "E45", {"start": v(9434.62, 0) * mm, "end": v(9239.75, 0) * mm});
            skLineSegment(sketch, "E46", {"start": v(9239.75, 190.5) * mm, "end": v(11195.55, 1524) * mm, "construction": true});
            skPoint(sketch, "E47", {"position": v(9337.18, 0) * mm});
            skLineSegment(sketch, "E48", {"start": v(9239.75, 190.5) * mm, "end": v(9239.75, 0) * mm});
            skLineSegment(sketch, "E49", {"start": v(9434.62, 0) * mm, "end": v(11930.6, 1701.8) * mm});
            skLineSegment(sketch, "E50", {"start": v(11930.6, 1701.8) * mm, "end": v(11474.95, 1701.8) * mm});
            skLineSegment(sketch, "E51", {"start": v(11474.95, 1701.8) * mm, "end": v(11474.95, 1524) * mm});
            skSolve(sketch);
        }
        {
            var Q0;
            Q0=qSketchRegion(id+"F12",true);
            var Q1;
            Q1=makeQuery(id+"F11.boolean.opBoolean","COPY",FACE,{"derivedFrom":makeQuery(id+"F11.opExtrude","SWEPT_FACE",FACE,{"disambiguationData":[OSD([sQuery(id+"F10.wireOp",EDGE,"E29.top")])]})});
            extrude(context, id + "F13", {"entities" : qUnion([Q0]), "operationType" : NewBodyOperationType.ADD, "endBound" : BoundingType.UP_TO_SURFACE, "oppositeDirection" : true, "depth" : 25.4 * mm, "endBoundEntityFace" : qUnion([Q1]), "offsetDistance" : 25.4 * mm});
        }
        {
            var Q0;
            Q0=makeQuery(id+"F9.boolean.opBoolean","MERGE",FACE,{"derivedFrom":[makeQuery(id+"F7.boolean.opBoolean","MERGE",FACE,{"derivedFrom":[makeQuery(id+"F5.boolean.opBoolean","MERGE",FACE,{"derivedFrom":[makeQuery(id+"F3.opExtrude","CAP_FACE",FACE,{"disambiguationData":[OSD([sQuery(id+"F2.wireOp",EDGE,"E8.0"),sQuery(id+"F2.wireOp",EDGE,"E9.0"),sQuery(id+"F2.wireOp",EDGE,"E9.1"),sQuery(id+"F2.wireOp",EDGE,"E10"),sQuery(id+"F2.wireOp",EDGE,"E11"),sQuery(id+"F2.wireOp",EDGE,"E12"),sQuery(id+"F2.wireOp",EDGE,"E14.0"),sQuery(id+"F2.wireOp",EDGE,"E14.1"),sQuery(id+"F2.wireOp",EDGE,"E14.2"),sQuery(id+"F2.wireOp",EDGE,"E14.3"),sQuery(id+"F2.wireOp",EDGE,"E14.4"),sQuery(id+"F2.wireOp",EDGE,"E14.5")])],"isStart":false}),makeQuery(id+"F5.opExtrude","CAP_FACE",FACE,{"disambiguationData":[OSD([sQuery(id+"F4.wireOp",EDGE,"E15.bottom"),sQuery(id+"F4.wireOp",EDGE,"E15.top"),sQuery(id+"F4.wireOp",EDGE,"E15.left"),sQuery(id+"F4.wireOp",EDGE,"E15.right")])],"isStart":false})]}),makeQuery(id+"F7.opExtrude","CAP_FACE",FACE,{"disambiguationData":[OSD([sQuery(id+"F6.wireOp",EDGE,"E16.bottom"),sQuery(id+"F6.wireOp",EDGE,"E16.top"),sQuery(id+"F6.wireOp",EDGE,"E16.left"),sQuery(id+"F6.wireOp",EDGE,"E16.right")])],"isStart":false}),makeQuery(id+"F7.opExtrude","CAP_FACE",FACE,{"disambiguationData":[OSD([sQuery(id+"F6.wireOp",EDGE,"E17.1.0.0"),sQuery(id+"F6.wireOp",EDGE,"E17.1.0.1"),sQuery(id+"F6.wireOp",EDGE,"E17.1.0.2"),sQuery(id+"F6.wireOp",EDGE,"E17.1.0.3")])],"isStart":false}),makeQuery(id+"F7.opExtrude","CAP_FACE",FACE,{"disambiguationData":[OSD([sQuery(id+"F6.wireOp",EDGE,"E17.2.0.0"),sQuery(id+"F6.wireOp",EDGE,"E17.2.0.1"),sQuery(id+"F6.wireOp",EDGE,"E17.2.0.2"),sQuery(id+"F6.wireOp",EDGE,"E17.2.0.3")])],"isStart":false}),makeQuery(id+"F7.opExtrude","CAP_FACE",FACE,{"disambiguationData":[OSD([sQuery(id+"F6.wireOp",EDGE,"E17.3.0.0"),sQuery(id+"F6.wireOp",EDGE,"E17.3.0.1"),sQuery(id+"F6.wireOp",EDGE,"E17.3.0.2"),sQuery(id+"F6.wireOp",EDGE,"E17.3.0.3")])],"isStart":false}),makeQuery(id+"F7.opExtrude","CAP_FACE",FACE,{"disambiguationData":[OSD([sQuery(id+"F6.wireOp",EDGE,"E17.4.0.0"),sQuery(id+"F6.wireOp",EDGE,"E17.4.0.1"),sQuery(id+"F6.wireOp",EDGE,"E17.4.0.2"),sQuery(id+"F6.wireOp",EDGE,"E17.4.0.3")])],"isStart":false}),makeQuery(id+"F7.opExtrude","CAP_FACE",FACE,{"disambiguationData":[OSD([sQuery(id+"F6.wireOp",EDGE,"E17.5.0.0"),sQuery(id+"F6.wireOp",EDGE,"E17.5.0.1"),sQuery(id+"F6.wireOp",EDGE,"E17.5.0.2"),sQuery(id+"F6.wireOp",EDGE,"E17.5.0.3")])],"isStart":false}),makeQuery(id+"F7.opExtrude","CAP_FACE",FACE,{"disambiguationData":[OSD([sQuery(id+"F6.wireOp",EDGE,"E17.6.0.0"),sQuery(id+"F6.wireOp",EDGE,"E17.6.0.1"),sQuery(id+"F6.wireOp",EDGE,"E17.6.0.2"),sQuery(id+"F6.wireOp",EDGE,"E17.6.0.3")])],"isStart":false}),makeQuery(id+"F7.opExtrude","CAP_FACE",FACE,{"disambiguationData":[OSD([sQuery(id+"F6.wireOp",EDGE,"E17.7.0.0"),sQuery(id+"F6.wireOp",EDGE,"E17.7.0.1"),sQuery(id+"F6.wireOp",EDGE,"E17.7.0.2"),sQuery(id+"F6.wireOp",EDGE,"E17.7.0.3")])],"isStart":false}),makeQuery(id+"F7.opExtrude","CAP_FACE",FACE,{"disambiguationData":[OSD([sQuery(id+"F6.wireOp",EDGE,"E17.8.0.0"),sQuery(id+"F6.wireOp",EDGE,"E17.8.0.1"),sQuery(id+"F6.wireOp",EDGE,"E17.8.0.2"),sQuery(id+"F6.wireOp",EDGE,"E17.8.0.3")])],"isStart":false}),makeQuery(id+"F7.opExtrude","CAP_FACE",FACE,{"disambiguationData":[OSD([sQuery(id+"F6.wireOp",EDGE,"E17.9.0.0"),sQuery(id+"F6.wireOp",EDGE,"E17.9.0.1"),sQuery(id+"F6.wireOp",EDGE,"E17.9.0.2"),sQuery(id+"F6.wireOp",EDGE,"E17.9.0.3")])],"isStart":false}),makeQuery(id+"F7.opExtrude","CAP_FACE",FACE,{"disambiguationData":[OSD([sQuery(id+"F6.wireOp",EDGE,"E18.top"),sQuery(id+"F6.wireOp",EDGE,"E18.left"),sQuery(id+"F6.wireOp",EDGE,"E18.right"),sQuery(id+"F6.wireOp",EDGE,"E20")])],"isStart":false}),makeQuery(id+"F7.opExtrude","CAP_FACE",FACE,{"disambiguationData":[OSD([sQuery(id+"F6.wireOp",EDGE,"E19.top"),sQuery(id+"F6.wireOp",EDGE,"E19.left"),sQuery(id+"F6.wireOp",EDGE,"E19.right"),sQuery(id+"F6.wireOp",EDGE,"E21.trimOffspring")])],"isStart":false})]}),makeQuery(id+"F9.opExtrude","CAP_FACE",FACE,{"disambiguationData":[OSD([sQuery(id+"F8.wireOp",EDGE,"E22"),sQuery(id+"F8.wireOp",EDGE,"E23"),sQuery(id+"F8.wireOp",EDGE,"E24"),sQuery(id+"F8.wireOp",EDGE,"E25"),sQuery(id+"F8.wireOp",EDGE,"E26"),sQuery(id+"F8.wireOp",EDGE,"E27"),sQuery(id+"F8.wireOp",EDGE,"E28")])],"isStart":true})]});
            var sketch = newSketch(context, id + "F14", { "sketchPlane" : qUnion([Q0])});
            skLineSegment(sketch, "E52.bottom", {"start": v(9239.75, -3042.15) * mm, "end": v(8630.15, -3042.15) * mm});
            skLineSegment(sketch, "E52.top", {"start": v(9239.75, -2026.15) * mm, "end": v(8630.15, -2026.15) * mm});
            skLineSegment(sketch, "E52.left", {"start": v(9239.75, -3042.15) * mm, "end": v(9239.75, -2026.15) * mm});
            skLineSegment(sketch, "E53", {"start": v(8630.15, -2026.15) * mm, "end": v(7614.15, -3042.15) * mm});
            skLineSegment(sketch, "E54", {"start": v(7614.15, -3042.15) * mm, "end": v(8630.15, -3042.15) * mm});
            skSolve(sketch);
        }
        {
            var Q0;
            Q0=qSketchRegion(id+"F14",true);
            extrude(context, id + "F15", {"entities" : qUnion([Q0]), "operationType" : NewBodyOperationType.REMOVE, "endBound" : BoundingType.UP_TO_NEXT, "oppositeDirection" : true, "depth" : 25.4 * mm, "offsetDistance" : 25.4 * mm});
        }
    });
